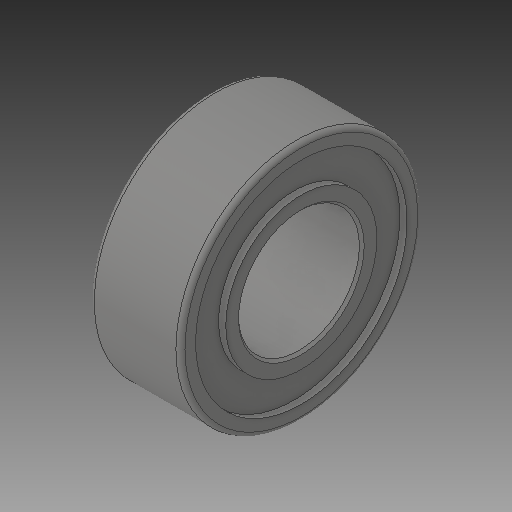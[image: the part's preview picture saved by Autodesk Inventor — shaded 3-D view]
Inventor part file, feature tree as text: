
AUTODESK INVENTOR PART (.ipt)
format: ipt  version: 2017 (Build 210142000, 142)  size: 162,304 bytes
history: native  units: in
note: dims shown in document units (in); Inventor stores cm internally (conversion verified against a paired STEP export)
features: chamfer x1
ambient origin geometry x8: Origin, YZ Plane, XZ Plane, XY Plane, X Axis, Y Axis, Z Axis, Center Point
bodies: Solid1 (feature_tree)
feature tree (1):
  chamfer  "Chamfer1"  [1 undecoded]
note: 1 required parameter value undecoded (feature->parameter linkage not recoverable at this tier; creation-order binding heuristic only, values carry confidence <= 0.55)
